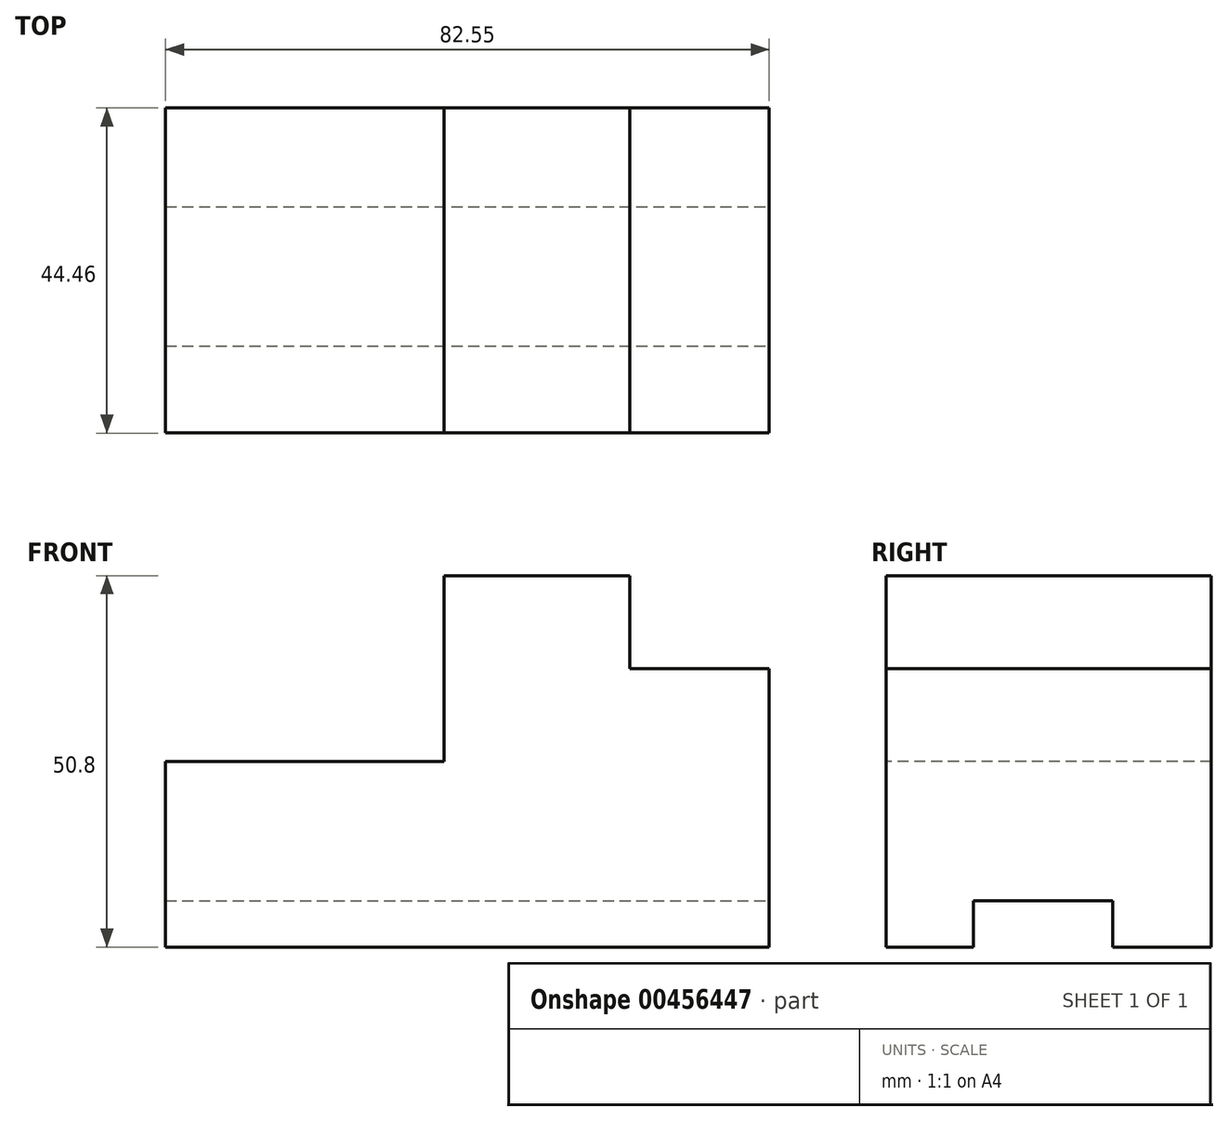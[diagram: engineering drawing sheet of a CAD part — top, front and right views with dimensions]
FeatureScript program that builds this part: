
annotation { "Feature Type Name" : "Feature", "Feature Type Description" : "" }
export const myFeature = defineFeature(function(context is Context, id is Id, definition is map)
    precondition{}
    {
        {
            var Q0;
            Q0=qCreatedBy(makeId("Front.planeOp"),FACE);
            var sketch = newSketch(context, id + "F0", { "sketchPlane" : qUnion([Q0])});
            skLineSegment(sketch, "E0.bottom", {"start": v(-41.38, -45.97) * mm, "end": v(41.17, -45.97) * mm});
            skLineSegment(sketch, "E0.top", {"start": v(-3.28, 4.83) * mm, "end": v(22.12, 4.83) * mm});
            skLineSegment(sketch, "E0.left", {"start": v(-41.38, -45.97) * mm, "end": v(-41.38, -20.57) * mm});
            skLineSegment(sketch, "E0.right", {"start": v(41.17, -45.97) * mm, "end": v(41.17, -7.87) * mm});
            skLineSegment(sketch, "E1.top", {"start": v(41.17, -7.87) * mm, "end": v(22.12, -7.87) * mm});
            skLineSegment(sketch, "E1.right", {"start": v(22.12, 4.83) * mm, "end": v(22.12, -7.87) * mm});
            skLineSegment(sketch, "E2.top", {"start": v(-41.38, -20.57) * mm, "end": v(-3.28, -20.57) * mm});
            skLineSegment(sketch, "E2.right", {"start": v(-3.28, 4.83) * mm, "end": v(-3.28, -20.57) * mm});
            skPoint(sketch, "E3.orphan", {"position": v(-41.38, 4.83) * mm});
            skSolve(sketch);
        }
        {
            var Q0;
            Q0=makeQuery(id+"F0.imprint","IMPRINT",FACE,{"disambiguationData":[TD([[makeQuery(id+"F0.imprint","IMPRINT",EDGE,{"derivedFrom":sQuery(id+"F0.wireOp",EDGE,"E0.bottom")}),1.0]])]});
            extrude(context, id + "F1", {"entities" : qUnion([Q0]), "endBound" : BoundingType.SYMMETRIC, "oppositeDirection" : true, "depth" : 44.45 * mm});
        }
        {
            var Q0;
            Q0=makeQuery(id+"F1.opExtrude","SWEPT_FACE",FACE,{"disambiguationData":[OSD([sQuery(id+"F0.wireOp",EDGE,"E0.right")])]});
            var sketch = newSketch(context, id + "F2", { "sketchPlane" : qUnion([Q0])});
            skLineSegment(sketch, "E4.bottom", {"start": v(-10.32, -45.97) * mm, "end": v(8.73, -45.97) * mm});
            skLineSegment(sketch, "E4.top", {"start": v(-10.32, -39.62) * mm, "end": v(8.73, -39.62) * mm});
            skLineSegment(sketch, "E4.left", {"start": v(-10.32, -45.97) * mm, "end": v(-10.32, -39.62) * mm});
            skLineSegment(sketch, "E4.right", {"start": v(8.73, -45.97) * mm, "end": v(8.73, -39.62) * mm});
            skSolve(sketch);
        }
        {
            var Q0;
            Q0=makeQuery(id+"F2.imprint","IMPRINT",FACE,{"disambiguationData":[TD([[makeQuery(id+"F2.imprint","IMPRINT",EDGE,{"derivedFrom":sQuery(id+"F2.wireOp",EDGE,"E4.bottom")}),-1.0]])]});
            extrude(context, id + "F3", {"entities" : qUnion([Q0]), "operationType" : NewBodyOperationType.REMOVE, "oppositeDirection" : true, "depth" : 82.55 * mm});
        }
    });
